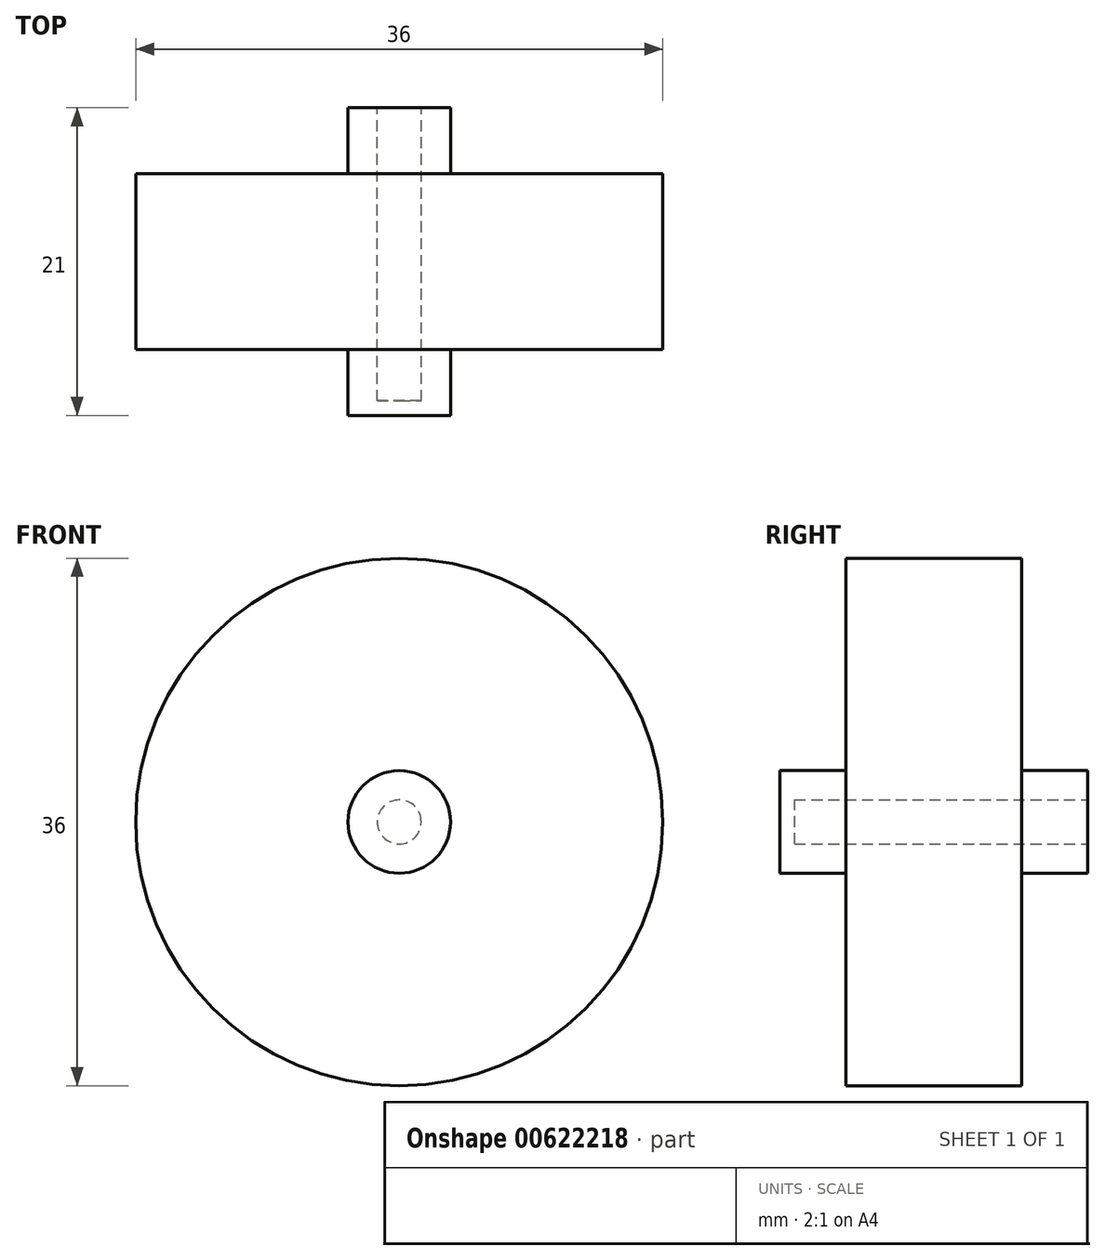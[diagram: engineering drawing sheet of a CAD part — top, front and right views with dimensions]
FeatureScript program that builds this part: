
annotation { "Feature Type Name" : "Feature", "Feature Type Description" : "" }
export const myFeature = defineFeature(function(context is Context, id is Id, definition is map)
    precondition{}
    {
        {
            var Q0;
            Q0=qCreatedBy(makeId("Front.planeOp"),FACE);
            var sketch = newSketch(context, id + "F0", { "sketchPlane" : qUnion([Q0])});
            skCircle(sketch, "E0", {"center": v(0, 0) * mm, "radius": 18 * mm});
            skCircle(sketch, "E1", {"center": v(0, 0) * mm, "radius": 3.5 * mm});
            skCircle(sketch, "E2", {"center": v(0, 0) * mm, "radius": 1.5 * mm});
            skSolve(sketch);
        }
        {
            var Q0;
            Q0=makeQuery(id+"F0.imprint","IMPRINT",FACE,{"disambiguationData":[TD([[makeQuery(id+"F0.imprint","IMPRINT",EDGE,{"derivedFrom":sQuery(id+"F0.wireOp",EDGE,"E0")}),1.0]])]});
            extrude(context, id + "F1", {"entities" : qUnion([Q0]), "depth" : 12 * mm, "offsetDistance" : 25 * mm});
        }
        {
            var Q0;
            Q0=makeQuery(id+"F0.imprint","IMPRINT",FACE,{"disambiguationData":[TD([[makeQuery(id+"F0.imprint","IMPRINT",EDGE,{"derivedFrom":sQuery(id+"F0.wireOp",EDGE,"E1")}),1.0]])]});
            extrude(context, id + "F2", {"entities" : qUnion([Q0]), "operationType" : NewBodyOperationType.ADD, "depth" : 16.5 * mm, "offsetDistance" : 25 * mm});
        }
        {
            var Q0;
            Q0=makeQuery(id+"F2.opExtrude","CAP_FACE",FACE,{"disambiguationData":[OSD([sQuery(id+"F0.wireOp",EDGE,"E1"),sQuery(id+"F0.wireOp",EDGE,"E2")])],"isStart":false});
            extrude(context, id + "F3", {"entities" : qUnion([Q0]), "operationType" : NewBodyOperationType.ADD, "oppositeDirection" : true, "depth" : 21 * mm, "offsetDistance" : 25 * mm});
        }
        {
            var Q0;
            Q0=makeQuery(id+"F2.opExtrude","CAP_FACE",FACE,{"disambiguationData":[OSD([sQuery(id+"F0.wireOp",EDGE,"E1"),sQuery(id+"F0.wireOp",EDGE,"E2")])],"isStart":false});
            var sketch = newSketch(context, id + "F4", { "sketchPlane" : qUnion([Q0])});
            skCircle(sketch, "E3", {"center": v(0, 0) * mm, "radius": 2.52 * mm});
            skSolve(sketch);
        }
        {
            var Q0;
            Q0=qSketchRegion(id+"F4",true);
            extrude(context, id + "F5", {"entities" : qUnion([Q0]), "operationType" : NewBodyOperationType.ADD, "oppositeDirection" : true, "depth" : 1 * mm});
        }
    });
